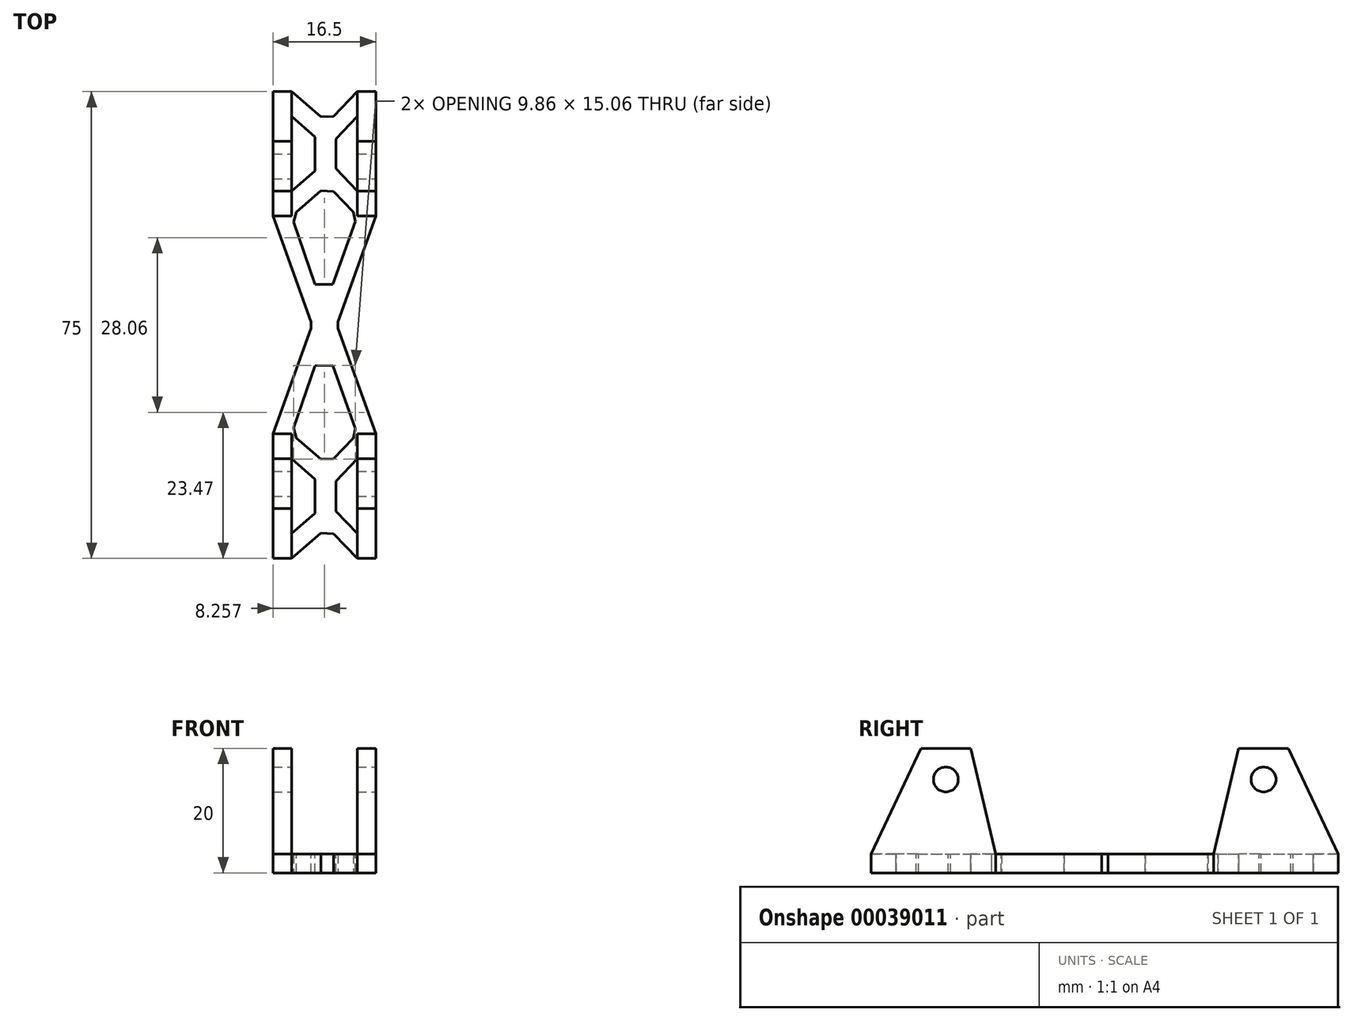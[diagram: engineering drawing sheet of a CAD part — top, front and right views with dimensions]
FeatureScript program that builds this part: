
annotation { "Feature Type Name" : "Feature", "Feature Type Description" : "" }
export const myFeature = defineFeature(function(context is Context, id is Id, definition is map)
    precondition{}
    {
        {
            var Q0;
            Q0=qCreatedBy(makeId("Top.planeOp"),FACE);
            var sketch = newSketch(context, id + "F0", { "sketchPlane" : qUnion([Q0])});
            skLineSegment(sketch, "E0.rect.bottom", {"start": v(8.25, -37.5) * mm, "end": v(-8.25, -37.5) * mm});
            skLineSegment(sketch, "E0.rect.top", {"start": v(8.25, 37.5) * mm, "end": v(-8.25, 37.5) * mm});
            skLineSegment(sketch, "E0.rect.left", {"start": v(8.25, -37.5) * mm, "end": v(8.25, 37.5) * mm});
            skLineSegment(sketch, "E0.rect.right", {"start": v(-8.25, -37.5) * mm, "end": v(-8.25, 37.5) * mm});
            skPoint(sketch, "E0.rect.middle", {"position": v(0, 0) * mm});
            skSolve(sketch);
        }
        {
            var Q0;
            Q0 = qSketchRegion(id + "F0", true);
            extrude(context, id + "F1", {"entities" : qUnion([Q0]), "depth" : 3 * mm});
        }
        {
            var Q0;
            Q0=makeQuery(id+"F1.opExtrude","CAP_FACE",FACE,{"disambiguationData":[OSD([sQuery(id+"F0.wireOp",EDGE,"E0.rect.bottom"),sQuery(id+"F0.wireOp",EDGE,"E0.rect.top"),sQuery(id+"F0.wireOp",EDGE,"E0.rect.left"),sQuery(id+"F0.wireOp",EDGE,"E0.rect.right")])],"isStart":false});
            var sketch = newSketch(context, id + "F2", { "sketchPlane" : qUnion([Q0])});
            skLineSegment(sketch, "E1.0", {"start": v(-5.25, -37.5) * mm, "end": v(-5.25, 37.5) * mm});
            skLineSegment(sketch, "E2.0", {"start": v(5.25, -37.5) * mm, "end": v(5.25, 37.5) * mm});
            skLineSegment(sketch, "E3", {"start": v(-5.25, 37.5) * mm, "end": v(-8.25, 37.5) * mm});
            skLineSegment(sketch, "E4", {"start": v(-8.25, 37.5) * mm, "end": v(-8.25, -37.5) * mm});
            skLineSegment(sketch, "E5", {"start": v(-8.25, -37.5) * mm, "end": v(-5.25, -37.5) * mm});
            skLineSegment(sketch, "E6", {"start": v(5.25, -37.5) * mm, "end": v(8.25, -37.5) * mm});
            skLineSegment(sketch, "E7", {"start": v(8.25, -37.5) * mm, "end": v(8.25, 37.5) * mm});
            skLineSegment(sketch, "E8", {"start": v(8.25, 37.5) * mm, "end": v(5.25, 37.5) * mm});
            skSolve(sketch);
        }
        {
            var Q0;
            Q0=makeQuery(id+"F2.imprint","IMPRINT",FACE,{"disambiguationData":[TD([[makeQuery(id+"F2.imprint","IMPRINT",EDGE,{"derivedFrom":sQuery(id+"F2.wireOp",EDGE,"E1.0")}),1.0]])]});
            var Q1;
            Q1=makeQuery(id+"F2.imprint","IMPRINT",FACE,{"disambiguationData":[TD([[makeQuery(id+"F2.imprint","IMPRINT",EDGE,{"derivedFrom":sQuery(id+"F2.wireOp",EDGE,"E2.0")}),-1.0]])]});
            extrude(context, id + "F3", {"entities" : qUnion([Q0, Q1]), "operationType" : NewBodyOperationType.ADD, "depth" : 17 * mm});
        }
        {
            var Q0;
            Q0=makeQuery(id+"F3.opExtrude","SWEPT_FACE",FACE,{"disambiguationData":[OSD([sQuery(id+"F2.wireOp",EDGE,"E1.0")])]});
            var sketch = newSketch(context, id + "F4", { "sketchPlane" : qUnion([Q0])});
            skLineSegment(sketch, "E9.0", {"start": v(-37.5, 3) * mm, "end": v(37.5, 3) * mm});
            skLineSegment(sketch, "E10.0", {"start": v(-32.5, 25) * mm, "end": v(-32.5, 0) * mm});
            skLineSegment(sketch, "E11.0", {"start": v(32.5, 25) * mm, "end": v(32.5, 0) * mm});
            skSolve(sketch);
        }
        {
            var Q0;
            Q0=makeQuery(id+"F3.boolean.opBoolean","MERGE",FACE,{"derivedFrom":[makeQuery(id+"F1.opExtrude","SWEPT_FACE",FACE,{"disambiguationData":[OSD([sQuery(id+"F0.wireOp",EDGE,"E0.rect.left")])]}),makeQuery(id+"F3.opExtrude","SWEPT_FACE",FACE,{"disambiguationData":[OSD([sQuery(id+"F2.wireOp",EDGE,"E7")])]})]});
            var sketch = newSketch(context, id + "F5", { "sketchPlane" : qUnion([Q0])});
            skLineSegment(sketch, "E12.0", {"start": v(-37.5, 3) * mm, "end": v(37.5, 3) * mm, "construction": true});
            skLineSegment(sketch, "E13", {"start": v(0, 0) * mm, "end": v(0, 20) * mm, "construction": true});
            skLineSegment(sketch, "E14", {"start": v(-37.5, 3) * mm, "end": v(-29.5, 20) * mm});
            skLineSegment(sketch, "E15", {"start": v(-21.5, 20) * mm, "end": v(-17.5, 3) * mm});
            skLineSegment(sketch, "E16", {"start": v(-29.5, 20) * mm, "end": v(-37.5, 20) * mm});
            skLineSegment(sketch, "E17.MirrorCS", {"start": v(21.5, 20) * mm, "end": v(17.5, 3) * mm});
            skLineSegment(sketch, "E18.MirrorCS", {"start": v(37.5, 3) * mm, "end": v(29.5, 20) * mm});
            skLineSegment(sketch, "E19.MirrorCS", {"start": v(29.5, 20) * mm, "end": v(37.5, 20) * mm});
            skLineSegment(sketch, "E20", {"start": v(-37.5, 20) * mm, "end": v(-37.5, 3) * mm});
            skLineSegment(sketch, "E21.MirrorCS", {"start": v(37.5, 20) * mm, "end": v(37.5, 3) * mm});
            skLineSegment(sketch, "E22", {"start": v(-17.5, 3) * mm, "end": v(17.5, 3) * mm});
            skLineSegment(sketch, "E23", {"start": v(-21.5, 20) * mm, "end": v(21.5, 20) * mm});
            skLineSegment(sketch, "E24", {"start": v(-29.5, 20) * mm, "end": v(-21.5, 20) * mm});
            skLineSegment(sketch, "E25", {"start": v(-25.5, 20) * mm, "end": v(-25.5, 15) * mm, "construction": true});
            skCircle(sketch, "E26", {"center": v(-25.5, 15) * mm, "radius": 2 * mm});
            skLineSegment(sketch, "E27", {"start": v(21.5, 20) * mm, "end": v(29.5, 20) * mm});
            skLineSegment(sketch, "E28", {"start": v(25.5, 20) * mm, "end": v(25.5, 15) * mm, "construction": true});
            skCircle(sketch, "E29", {"center": v(25.5, 15) * mm, "radius": 2 * mm});
            skSolve(sketch);
        }
        {
            var Q0;
            Q0 = qSketchRegion(id + "F5", true);
            extrude(context, id + "F6", {"entities" : qUnion([Q0]), "operationType" : NewBodyOperationType.REMOVE, "oppositeDirection" : true, "depth" : 25 * mm});
        }
        {
            var Q0;
            Q0=makeQuery(id+"F6.boolean.opBoolean","MERGE",FACE,{"derivedFrom":[makeQuery(id+"F1.opExtrude","CAP_FACE",FACE,{"disambiguationData":[OSD([sQuery(id+"F0.wireOp",EDGE,"E0.rect.bottom"),sQuery(id+"F0.wireOp",EDGE,"E0.rect.top"),sQuery(id+"F0.wireOp",EDGE,"E0.rect.left"),sQuery(id+"F0.wireOp",EDGE,"E0.rect.right")])],"isStart":false}),makeQuery(id+"F6.opExtrude","SWEPT_FACE",FACE,{"disambiguationData":[OSD([sQuery(id+"F5.wireOp",EDGE,"E22")])]})]});
            var sketch = newSketch(context, id + "F7", { "sketchPlane" : qUnion([Q0])});
            skLineSegment(sketch, "E30", {"start": v(-2, 0) * mm, "end": v(-8.25, 17.5) * mm});
            skLineSegment(sketch, "E31", {"start": v(8.25, -17.5) * mm, "end": v(2, 0) * mm});
            skLineSegment(sketch, "E32", {"start": v(-2, 0) * mm, "end": v(-8.25, -17.5) * mm});
            skLineSegment(sketch, "E33", {"start": v(2, 0) * mm, "end": v(8.25, 17.5) * mm});
            skLineSegment(sketch, "E34", {"start": v(8.25, -17.5) * mm, "end": v(8.25, 17.5) * mm});
            skLineSegment(sketch, "E35", {"start": v(-8.25, -17.5) * mm, "end": v(-8.25, 17.5) * mm});
            skLineSegment(sketch, "E36", {"start": v(5.25, 17.5) * mm, "end": v(-0.12, 2.45) * mm});
            skLineSegment(sketch, "E37", {"start": v(-0.12, 2.45) * mm, "end": v(-5.25, 17.5) * mm});
            skLineSegment(sketch, "E38", {"start": v(5.25, -17.5) * mm, "end": v(-0.12, -2.45) * mm});
            skLineSegment(sketch, "E39", {"start": v(-0.12, -2.45) * mm, "end": v(-5.25, -17.5) * mm});
            skPoint(sketch, "E40.orphan", {"position": v(0, 37.5) * mm});
            skPoint(sketch, "E41.orphan", {"position": v(0, -37.5) * mm});
            skLineSegment(sketch, "E42", {"start": v(-5.25, 17.5) * mm, "end": v(0.5, 22.5) * mm});
            skLineSegment(sketch, "E43", {"start": v(5.25, 17.5) * mm, "end": v(0.5, 22.5) * mm});
            skLineSegment(sketch, "E44", {"start": v(-5.25, -17.5) * mm, "end": v(0.5, -22.5) * mm});
            skLineSegment(sketch, "E45", {"start": v(0.5, -22.5) * mm, "end": v(5.25, -17.5) * mm});
            skLineSegment(sketch, "E46", {"start": v(0.5, -32.5) * mm, "end": v(5.25, -37.5) * mm});
            skLineSegment(sketch, "E47", {"start": v(0.5, -32.5) * mm, "end": v(-5.25, -37.5) * mm});
            skLineSegment(sketch, "E48", {"start": v(-5.25, -37.5) * mm, "end": v(5.25, -37.5) * mm});
            skLineSegment(sketch, "E49", {"start": v(-5.25, 37.5) * mm, "end": v(0.5, 32.5) * mm});
            skLineSegment(sketch, "E50", {"start": v(5.25, 37.5) * mm, "end": v(-5.25, 37.5) * mm});
            skLineSegment(sketch, "E51", {"start": v(0.5, 32.5) * mm, "end": v(5.25, 37.5) * mm});
            skLineSegment(sketch, "E52", {"start": v(-1.5, -24.76) * mm, "end": v(-5.25, -21.5) * mm});
            skLineSegment(sketch, "E53", {"start": v(1.83, -25.1) * mm, "end": v(5.25, -21.5) * mm});
            skLineSegment(sketch, "E54", {"start": v(-1.5, -30.24) * mm, "end": v(-5.25, -33.5) * mm});
            skLineSegment(sketch, "E55", {"start": v(1.83, -29.9) * mm, "end": v(5.25, -33.5) * mm});
            skLineSegment(sketch, "E56", {"start": v(-5.25, -21.5) * mm, "end": v(-5.25, -33.5) * mm});
            skLineSegment(sketch, "E57", {"start": v(5.25, -21.5) * mm, "end": v(5.25, -33.5) * mm});
            skLineSegment(sketch, "E58", {"start": v(-1.5, 24.76) * mm, "end": v(-5.25, 21.5) * mm});
            skLineSegment(sketch, "E59", {"start": v(1.83, 25.1) * mm, "end": v(5.25, 21.5) * mm});
            skLineSegment(sketch, "E60", {"start": v(-1.5, 30.24) * mm, "end": v(-5.25, 33.5) * mm});
            skLineSegment(sketch, "E61", {"start": v(1.83, 29.9) * mm, "end": v(5.25, 33.5) * mm});
            skLineSegment(sketch, "E62", {"start": v(5.25, 33.5) * mm, "end": v(5.25, 21.5) * mm});
            skLineSegment(sketch, "E63", {"start": v(-5.25, 21.5) * mm, "end": v(-5.25, 33.5) * mm});
            skLineSegment(sketch, "E64.0.left", {"start": v(-1.5, -30.24) * mm, "end": v(-1.5, -24.76) * mm});
            skLineSegment(sketch, "E64.0.right", {"start": v(1.83, -29.9) * mm, "end": v(1.83, -25.1) * mm});
            skLineSegment(sketch, "E64.1.left", {"start": v(-1.5, 24.76) * mm, "end": v(-1.5, 30.24) * mm});
            skLineSegment(sketch, "E64.1.right", {"start": v(1.83, 25.1) * mm, "end": v(1.83, 29.9) * mm});
            skSolve(sketch);
        }
        {
            var Q0;
            Q0 = qSketchRegion(id + "F7", true);
            var Q1;
            Q1=makeQuery(id+"F1.opExtrude","CAP_FACE",FACE,{"disambiguationData":[OSD([sQuery(id+"F0.wireOp",EDGE,"E0.rect.bottom"),sQuery(id+"F0.wireOp",EDGE,"E0.rect.top"),sQuery(id+"F0.wireOp",EDGE,"E0.rect.left"),sQuery(id+"F0.wireOp",EDGE,"E0.rect.right")])],"isStart":true});
            extrude(context, id + "F8", {"entities" : qUnion([Q0]), "operationType" : NewBodyOperationType.REMOVE, "endBound" : BoundingType.UP_TO_SURFACE, "oppositeDirection" : true, "endBoundEntityFace" : qUnion([Q1]), "depth" : 25 * mm});
        }
        {
            var Q0;
            Q0=makeQuery(id+"F8.boolean.opBoolean","COPY",EDGE,{"derivedFrom":makeQuery(id+"F8.opExtrude","SWEPT_EDGE",EDGE,{"disambiguationData":[OSD([sQuery(id+"F2.wireOp",EDGE,"E1.0"),sQuery(id+"F5.wireOp",EDGE,"E15"),sQuery(id+"F5.wireOp",EDGE,"E22"),sQuery(id+"F7.wireOp",EDGE,"E39"),sQuery(id+"F7.wireOp",EDGE,"E44")])]})});
            var Q1;
            Q1=makeQuery(id+"F8.boolean.opBoolean","COPY",EDGE,{"derivedFrom":makeQuery(id+"F8.opExtrude","SWEPT_EDGE",EDGE,{"disambiguationData":[OSD([sQuery(id+"F7.wireOp",EDGE,"E44"),sQuery(id+"F7.wireOp",EDGE,"E45")])]})});
            var Q2;
            Q2=makeQuery(id+"F8.boolean.opBoolean","COPY",EDGE,{"derivedFrom":makeQuery(id+"F8.opExtrude","SWEPT_EDGE",EDGE,{"disambiguationData":[OSD([sQuery(id+"F7.wireOp",EDGE,"E38"),sQuery(id+"F7.wireOp",EDGE,"E39")])]})});
            var Q3;
            Q3=makeQuery(id+"F8.boolean.opBoolean","COPY",EDGE,{"derivedFrom":makeQuery(id+"F8.opExtrude","SWEPT_EDGE",EDGE,{"disambiguationData":[OSD([sQuery(id+"F2.wireOp",EDGE,"E2.0"),sQuery(id+"F5.wireOp",EDGE,"E15"),sQuery(id+"F5.wireOp",EDGE,"E22"),sQuery(id+"F7.wireOp",EDGE,"E38"),sQuery(id+"F7.wireOp",EDGE,"E45")])]})});
            var Q4;
            Q4=makeQuery(id+"F8.boolean.opBoolean","COPY",EDGE,{"derivedFrom":makeQuery(id+"F8.opExtrude","SWEPT_EDGE",EDGE,{"disambiguationData":[OSD([sQuery(id+"F2.wireOp",EDGE,"E1.0"),sQuery(id+"F5.wireOp",EDGE,"E17.MirrorCS"),sQuery(id+"F5.wireOp",EDGE,"E22"),sQuery(id+"F7.wireOp",EDGE,"E37"),sQuery(id+"F7.wireOp",EDGE,"E42")])]})});
            var Q5;
            Q5=makeQuery(id+"F8.boolean.opBoolean","COPY",EDGE,{"derivedFrom":makeQuery(id+"F8.opExtrude","SWEPT_EDGE",EDGE,{"disambiguationData":[OSD([sQuery(id+"F7.wireOp",EDGE,"E42"),sQuery(id+"F7.wireOp",EDGE,"E43")])]})});
            var Q6;
            Q6=makeQuery(id+"F8.boolean.opBoolean","COPY",EDGE,{"derivedFrom":makeQuery(id+"F8.opExtrude","SWEPT_EDGE",EDGE,{"disambiguationData":[OSD([sQuery(id+"F7.wireOp",EDGE,"E36"),sQuery(id+"F7.wireOp",EDGE,"E37")])]})});
            var Q7;
            Q7=makeQuery(id+"F8.boolean.opBoolean","COPY",EDGE,{"derivedFrom":makeQuery(id+"F8.opExtrude","SWEPT_EDGE",EDGE,{"disambiguationData":[OSD([sQuery(id+"F2.wireOp",EDGE,"E2.0"),sQuery(id+"F5.wireOp",EDGE,"E17.MirrorCS"),sQuery(id+"F5.wireOp",EDGE,"E22"),sQuery(id+"F7.wireOp",EDGE,"E36"),sQuery(id+"F7.wireOp",EDGE,"E43")])]})});
            var Q8;
            Q8=makeQuery(id+"F8.boolean.opBoolean","COPY",EDGE,{"derivedFrom":makeQuery(id+"F8.opExtrude","SWEPT_EDGE",EDGE,{"disambiguationData":[OSD([sQuery(id+"F7.wireOp",EDGE,"E31"),sQuery(id+"F7.wireOp",EDGE,"E33")])]})});
            var Q9;
            Q9=makeQuery(id+"F8.boolean.opBoolean","COPY",EDGE,{"derivedFrom":makeQuery(id+"F8.opExtrude","SWEPT_EDGE",EDGE,{"disambiguationData":[OSD([sQuery(id+"F7.wireOp",EDGE,"E30"),sQuery(id+"F7.wireOp",EDGE,"E32")])]})});
            var Q10;
            Q10=makeQuery(id+"F8.boolean.opBoolean","COPY",EDGE,{"derivedFrom":makeQuery(id+"F8.opExtrude","SWEPT_EDGE",EDGE,{"disambiguationData":[OSD([sQuery(id+"F7.wireOp",EDGE,"E46"),sQuery(id+"F7.wireOp",EDGE,"E47")])]})});
            var Q11;
            Q11=makeQuery(id+"F8.boolean.opBoolean","COPY",EDGE,{"derivedFrom":makeQuery(id+"F8.opExtrude","SWEPT_EDGE",EDGE,{"disambiguationData":[OSD([sQuery(id+"F7.wireOp",EDGE,"E49"),sQuery(id+"F7.wireOp",EDGE,"E51")])]})});
            chamfer(context, id + "F9", {"entities" : qUnion([Q0, Q1, Q2, Q3, Q4, Q5, Q6, Q7, Q8, Q9, Q10, Q11]), "width" : 1.5 * mm, "tangentPropagation" : true});
        }
    });
